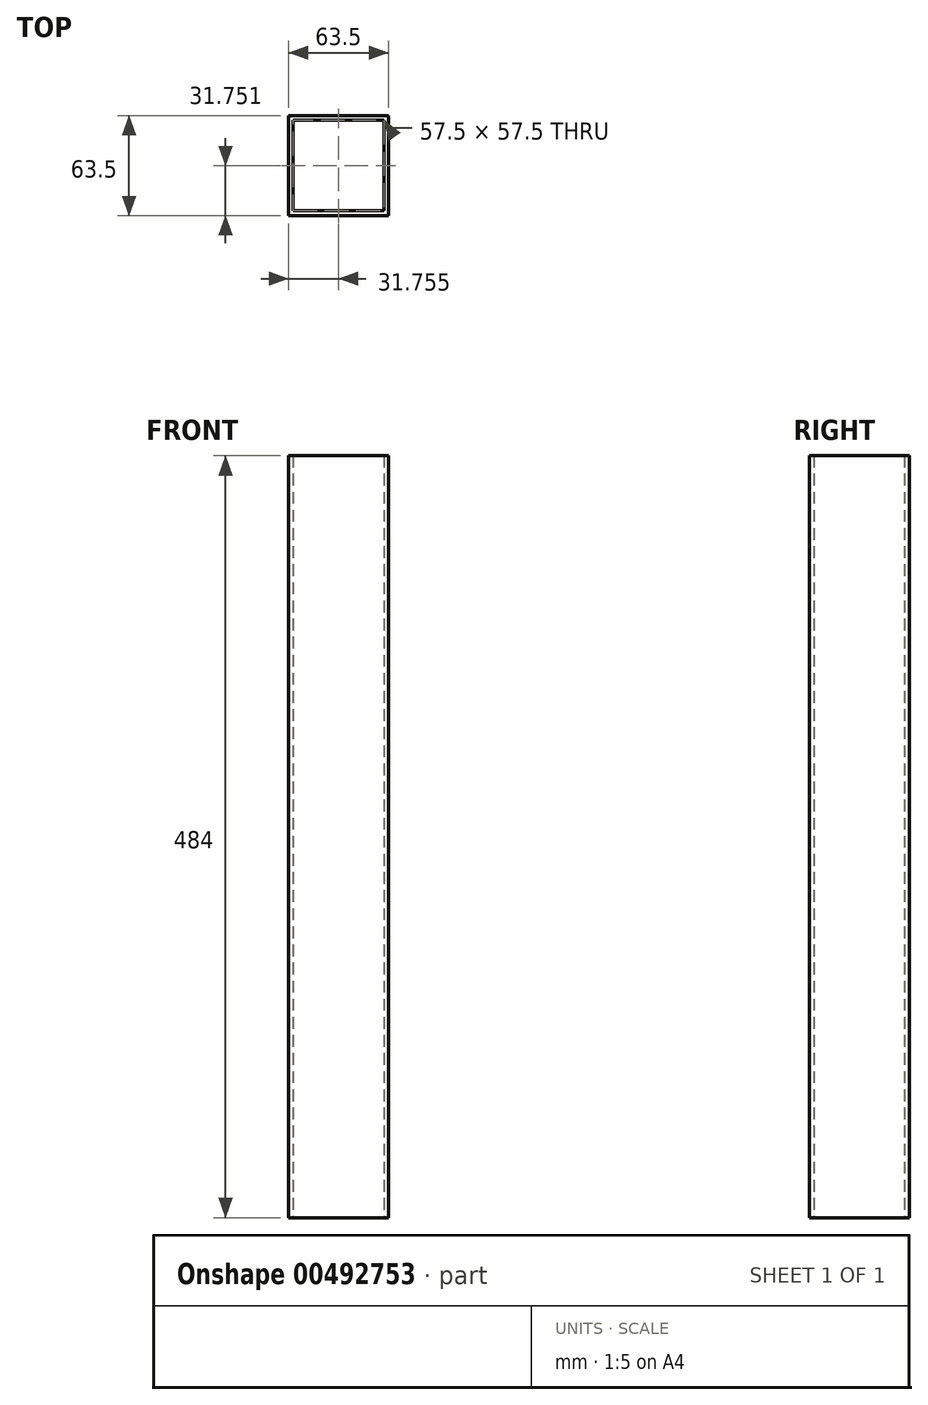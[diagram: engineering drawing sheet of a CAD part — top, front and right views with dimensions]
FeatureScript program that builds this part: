
annotation { "Feature Type Name" : "Feature", "Feature Type Description" : "" }
export const myFeature = defineFeature(function(context is Context, id is Id, definition is map)
    precondition{}
    {
        {
            var Q0;
            Q0=qCreatedBy(makeId("Top.planeOp"),FACE);
            var sketch = newSketch(context, id + "F0", { "sketchPlane" : qUnion([Q0])});
            skLineSegment(sketch, "E0.bottom", {"start": v(-25.8, 25.98) * mm, "end": v(31.7, 25.98) * mm});
            skLineSegment(sketch, "E0.top", {"start": v(-25.8, -31.52) * mm, "end": v(31.7, -31.52) * mm});
            skLineSegment(sketch, "E0.left", {"start": v(-25.8, 25.98) * mm, "end": v(-25.8, -31.52) * mm});
            skLineSegment(sketch, "E0.right", {"start": v(31.7, 25.98) * mm, "end": v(31.7, -31.52) * mm});
            skLineSegment(sketch, "E1.bottom", {"start": v(-28.8, 28.98) * mm, "end": v(34.7, 28.98) * mm});
            skLineSegment(sketch, "E1.top", {"start": v(-28.8, -34.52) * mm, "end": v(34.7, -34.52) * mm});
            skLineSegment(sketch, "E1.left", {"start": v(-28.8, 28.98) * mm, "end": v(-28.8, -34.52) * mm});
            skLineSegment(sketch, "E1.right", {"start": v(34.7, 28.98) * mm, "end": v(34.7, -34.52) * mm});
            skSolve(sketch);
        }
        {
            var Q0;
            Q0 = qSketchRegion(id + "F0", true);
            extrude(context, id + "F1", {"entities" : qUnion([Q0]), "offsetDistance" : 25 * mm, "depth" : 484 * mm});
        }
    });
